# Revit family: Ascoli Swing
name_source: partatom
category: Lighting Fixtures
revit_build: Autodesk Revit 2018 (Build: 20170927_1515(x64)
units: mm (PartAtom-declared; Revit-internal decimal feet)

## family parameters
Always vertical = Yes
Cut with Voids When Loaded = No
Host = Wall
Light Source = No
OmniClass Number = 23.80.70.00
OmniClass Title = Lighting
Part Type = Normal
Room Calculation Point = No
Round Connector Dimension = Use Diameter
Shared = No

## types (2) — shared parameters
Dimmable = Yes
Dimming Method = Lamp Dependent
Driver Included = Not Applicable
Driver Required = No
Efficacy (lm/w) = Lamp Dependent
Lamp = GU10 LED
Main Finish = Various
Main Material = Metal - Mild Steel
Manufacturer = Astro Lighting Ltd
Power (Watts) = 6W Max
Product Location = Indoor
Product Name = Ascoli Swing
URL = www.astrolighting.com

## per-type parameters (varying)
| type | ADA compliant | Electrical Class | Light Source Fixed | Location rating | Product Code | Product SKU |
| CE | Not Applicable | 2 |  | IP20 | 0 | 1286066 |
| ETL | No | 1 | Yes | DAMP | 8644 | 1286068 |

## geometry (parser evidence)
native form markers: Sweep x2
no freeform markers — native parametric forms only
